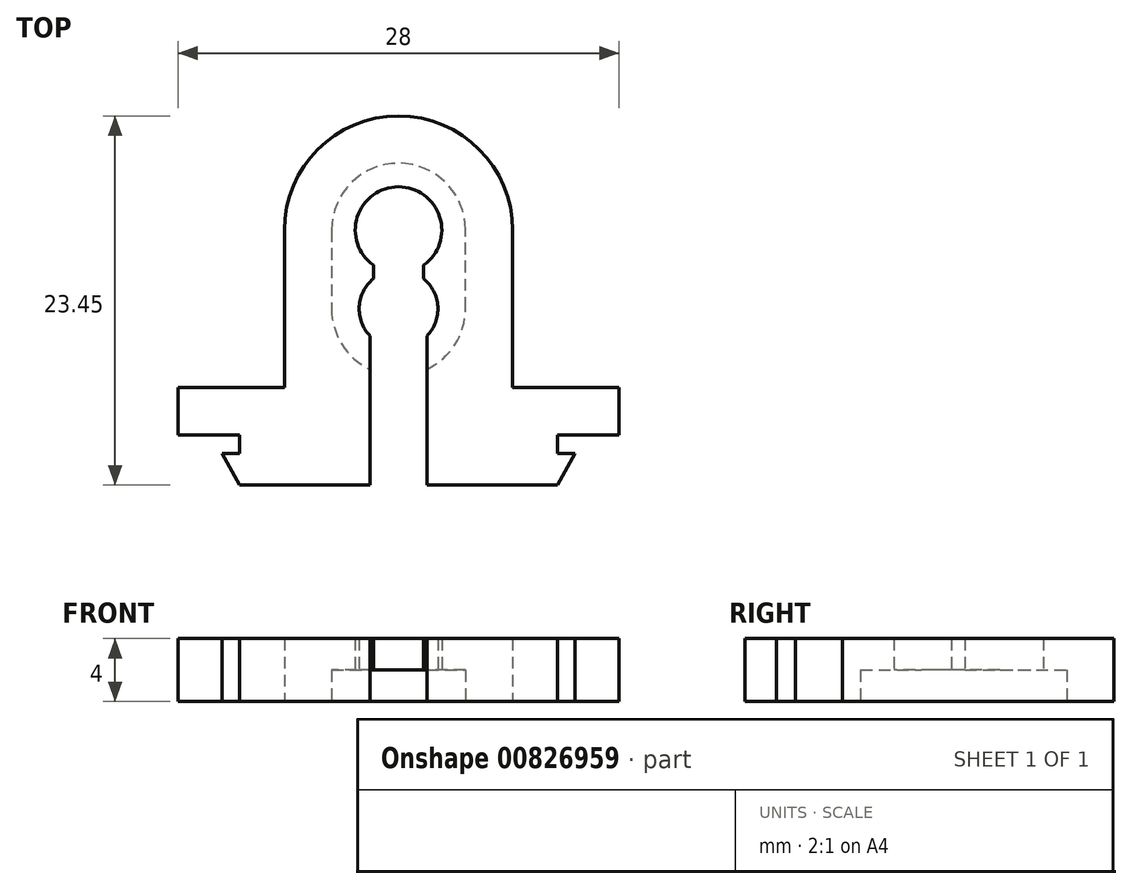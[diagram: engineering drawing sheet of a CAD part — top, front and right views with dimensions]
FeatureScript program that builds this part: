
annotation { "Feature Type Name" : "Feature", "Feature Type Description" : "" }
export const myFeature = defineFeature(function(context is Context, id is Id, definition is map)
    precondition{}
    {
        {
            var Q0;
            Q0=qCreatedBy(makeId("Top.planeOp"),FACE);
            var sketch = newSketch(context, id + "F0", { "sketchPlane" : qUnion([Q0])});
            skArc(sketch, "E0", {"start": v(1.6, -2.24) * mm, "mid": v(2.62, 0.84) * mm, "end": v(0, 2.75) * mm});
            skArc(sketch, "E1.0", {"start": v(4.25, 0) * mm, "mid": v(3, 3) * mm, "end": v(0, 4.25) * mm});
            skLineSegment(sketch, "E2", {"start": v(4.25, 0) * mm, "end": v(4.25, -2.5) * mm});
            skArc(sketch, "E3.MirrorCS", {"start": v(4.25, -5) * mm, "mid": v(3, -8) * mm, "end": v(0, -9.25) * mm});
            skLineSegment(sketch, "E4.MirrorCS", {"start": v(4.25, -5) * mm, "end": v(4.25, -2.5) * mm});
            skArc(sketch, "E5.MirrorCS", {"start": v(-1.6, -2.24) * mm, "mid": v(-2.62, 0.84) * mm, "end": v(0, 2.75) * mm});
            skLineSegment(sketch, "E6.MirrorCS", {"start": v(-4.25, 0) * mm, "end": v(-4.25, -2.5) * mm});
            skLineSegment(sketch, "E7.MirrorCS", {"start": v(-4.25, -5) * mm, "end": v(-4.25, -2.5) * mm});
            skArc(sketch, "E8.MirrorCS", {"start": v(-4.25, -5) * mm, "mid": v(-3, -8) * mm, "end": v(0, -9.25) * mm});
            skArc(sketch, "E9.MirrorCS", {"start": v(-4.25, 0) * mm, "mid": v(-3, 3) * mm, "end": v(0, 4.25) * mm});
            skLineSegment(sketch, "E10.0", {"start": v(-7.25, -5) * mm, "end": v(-7.25, -2.5) * mm});
            skLineSegment(sketch, "E10.1", {"start": v(-7.25, 0) * mm, "end": v(-7.25, -2.5) * mm});
            skLineSegment(sketch, "E10.2", {"start": v(7.25, -5) * mm, "end": v(7.25, -2.5) * mm});
            skLineSegment(sketch, "E10.3", {"start": v(7.25, 0) * mm, "end": v(7.25, -2.5) * mm});
            skArc(sketch, "E10.4", {"start": v(7.25, 0) * mm, "mid": v(5.13, 5.13) * mm, "end": v(0, 7.25) * mm});
            skArc(sketch, "E10.5", {"start": v(-7.25, 0) * mm, "mid": v(-5.13, 5.13) * mm, "end": v(0, 7.25) * mm});
            skLineSegment(sketch, "E11", {"start": v(7.25, -5) * mm, "end": v(7.25, -10) * mm});
            skLineSegment(sketch, "E12", {"start": v(7.25, -10) * mm, "end": v(14, -10) * mm});
            skLineSegment(sketch, "E13", {"start": v(14, -10) * mm, "end": v(14, -13) * mm});
            skLineSegment(sketch, "E14", {"start": v(14, -13) * mm, "end": v(10.1, -13) * mm});
            skLineSegment(sketch, "E15", {"start": v(10.1, -13) * mm, "end": v(10.1, -14.2) * mm});
            skLineSegment(sketch, "E16", {"start": v(10.1, -14.2) * mm, "end": v(11.2, -14.2) * mm});
            skLineSegment(sketch, "E17", {"start": v(11.2, -14.2) * mm, "end": v(10.1, -16.2) * mm});
            skLineSegment(sketch, "E18", {"start": v(10.1, -16.2) * mm, "end": v(1.8, -16.2) * mm});
            skLineSegment(sketch, "E19", {"start": v(1.8, -16.2) * mm, "end": v(1.8, -8.85) * mm});
            skLineSegment(sketch, "E20.MirrorCS", {"start": v(-10.1, -13) * mm, "end": v(-10.1, -14.2) * mm});
            skLineSegment(sketch, "E21.MirrorCS", {"start": v(-10.1, -14.2) * mm, "end": v(-11.2, -14.2) * mm});
            skLineSegment(sketch, "E22.MirrorCS", {"start": v(-1.8, -8.85) * mm, "end": v(-1.8, -8.85) * mm});
            skLineSegment(sketch, "E23.MirrorCS", {"start": v(-14, -10) * mm, "end": v(-14, -13) * mm});
            skLineSegment(sketch, "E24.MirrorCS", {"start": v(-11.2, -14.2) * mm, "end": v(-10.1, -16.2) * mm});
            skLineSegment(sketch, "E25.MirrorCS", {"start": v(-1.8, -16.2) * mm, "end": v(-1.8, -8.85) * mm});
            skLineSegment(sketch, "E26.MirrorCS", {"start": v(-7.25, -5) * mm, "end": v(-7.25, -10) * mm});
            skLineSegment(sketch, "E27.MirrorCS", {"start": v(-14, -13) * mm, "end": v(-10.1, -13) * mm});
            skLineSegment(sketch, "E28.MirrorCS", {"start": v(-10.1, -16.2) * mm, "end": v(-1.8, -16.2) * mm});
            skLineSegment(sketch, "E29.MirrorCS", {"start": v(-7.25, -10) * mm, "end": v(-14, -10) * mm});
            skLineSegment(sketch, "E30", {"start": v(-1.8, -8.85) * mm, "end": v(-1.8, -6.73) * mm});
            skLineSegment(sketch, "E31", {"start": v(1.8, -8.85) * mm, "end": v(1.8, -6.73) * mm});
            skLineSegment(sketch, "E32", {"start": v(-1.6, -2.24) * mm, "end": v(-1.6, -3.08) * mm});
            skLineSegment(sketch, "E33", {"start": v(1.6, -2.24) * mm, "end": v(1.6, -3.08) * mm});
            skArc(sketch, "E34", {"start": v(-1.6, -3.08) * mm, "mid": v(-2.5, -4.86) * mm, "end": v(-1.8, -6.73) * mm});
            skArc(sketch, "E35.MirrorCS", {"start": v(1.6, -3.08) * mm, "mid": v(2.5, -4.86) * mm, "end": v(1.8, -6.73) * mm});
            skSolve(sketch);
        }
        {
            var Q0;
            Q0=makeQuery(id+"F0.imprint","IMPRINT",FACE,{"disambiguationData":[TD([[makeQuery(id+"F0.imprint","IMPRINT",EDGE,{"derivedFrom":sQuery(id+"F0.wireOp",EDGE,"E1.0")}),-1.0]])]});
            extrude(context, id + "F1", {"entities" : qUnion([Q0]), "depth" : 4 * mm, "offsetDistance" : 25 * mm, "symmetric" : true});
        }
        {
            var Q0;
            Q0=makeQuery(id+"F0.imprint","IMPRINT",FACE,{"disambiguationData":[TD([[makeQuery(id+"F0.imprint","IMPRINT",EDGE,{"derivedFrom":sQuery(id+"F0.wireOp",EDGE,"E0")}),-1.0]])]});
            extrude(context, id + "F2", {"entities" : qUnion([Q0]), "operationType" : NewBodyOperationType.ADD, "depth" : 2 * mm, "offsetDistance" : 25 * mm});
        }
    });
